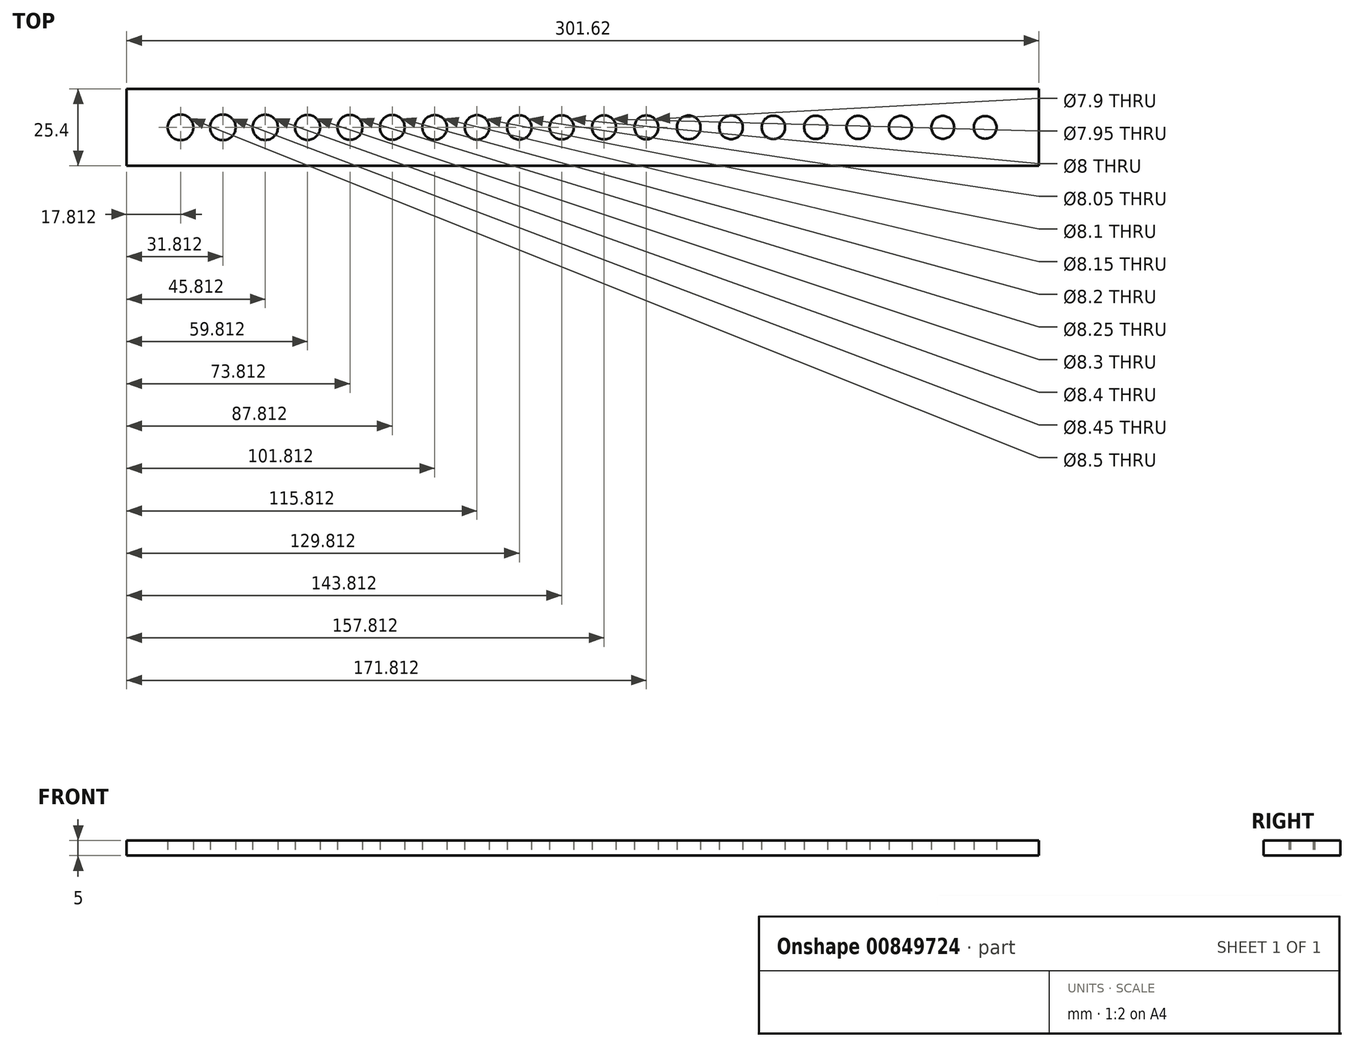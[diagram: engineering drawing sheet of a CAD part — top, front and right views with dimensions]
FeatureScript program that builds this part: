
annotation { "Feature Type Name" : "Feature", "Feature Type Description" : "" }
export const myFeature = defineFeature(function(context is Context, id is Id, definition is map)
    precondition{}
    {
        {
            var Q0;
            Q0=qCreatedBy(makeId("Top.planeOp"),FACE);
            var sketch = newSketch(context, id + "F0", { "sketchPlane" : qUnion([Q0])});
            skLineSegment(sketch, "E0.bottom", {"start": v(0, 0) * mm, "end": v(301.63, 0) * mm});
            skLineSegment(sketch, "E0.top", {"start": v(0, 25.4) * mm, "end": v(301.63, 25.4) * mm});
            skLineSegment(sketch, "E0.left", {"start": v(0, 0) * mm, "end": v(0, 25.4) * mm});
            skLineSegment(sketch, "E0.right", {"start": v(301.63, 0) * mm, "end": v(301.63, 25.4) * mm});
            skLineSegment(sketch, "E1", {"start": v(0, 12.7) * mm, "end": v(301.63, 12.7) * mm, "construction": true});
            skPoint(sketch, "E2", {"position": v(17.81, 12.7) * mm});
            skPoint(sketch, "E3.1.0.0", {"position": v(31.81, 12.7) * mm});
            skPoint(sketch, "E3.2.0.0", {"position": v(45.81, 12.7) * mm});
            skPoint(sketch, "E3.3.0.0", {"position": v(59.81, 12.7) * mm});
            skPoint(sketch, "E3.4.0.0", {"position": v(73.81, 12.7) * mm});
            skPoint(sketch, "E3.5.0.0", {"position": v(87.81, 12.7) * mm});
            skPoint(sketch, "E3.6.0.0", {"position": v(101.81, 12.7) * mm});
            skPoint(sketch, "E3.7.0.0", {"position": v(115.81, 12.7) * mm});
            skPoint(sketch, "E3.8.0.0", {"position": v(129.81, 12.7) * mm});
            skPoint(sketch, "E3.9.0.0", {"position": v(143.81, 12.7) * mm});
            skPoint(sketch, "E3.10.0.0", {"position": v(157.81, 12.7) * mm});
            skPoint(sketch, "E3.11.0.0", {"position": v(171.81, 12.7) * mm});
            skPoint(sketch, "E3.12.0.0", {"position": v(185.81, 12.7) * mm});
            skPoint(sketch, "E3.13.0.0", {"position": v(199.81, 12.7) * mm});
            skPoint(sketch, "E3.14.0.0", {"position": v(213.81, 12.7) * mm});
            skPoint(sketch, "E3.15.0.0", {"position": v(227.81, 12.7) * mm});
            skPoint(sketch, "E3.16.0.0", {"position": v(241.81, 12.7) * mm});
            skPoint(sketch, "E3.17.0.0", {"position": v(255.81, 12.7) * mm});
            skPoint(sketch, "E3.18.0.0", {"position": v(269.81, 12.7) * mm});
            skPoint(sketch, "E3.19.0.0", {"position": v(283.81, 12.7) * mm});
            skLineSegment(sketch, "E3.direction1", {"start": v(17.81, 12.7) * mm, "end": v(31.81, 12.7) * mm, "construction": true});
            skCircle(sketch, "E4", {"center": v(17.81, 12.7) * mm, "radius": 4.25 * mm});
            skCircle(sketch, "E5", {"center": v(31.81, 12.7) * mm, "radius": 4.22 * mm});
            skCircle(sketch, "E6", {"center": v(45.81, 12.7) * mm, "radius": 4.2 * mm});
            skCircle(sketch, "E7", {"center": v(59.81, 12.7) * mm, "radius": 4.15 * mm});
            skCircle(sketch, "E8", {"center": v(73.81, 12.7) * mm, "radius": 4.12 * mm});
            skCircle(sketch, "E9", {"center": v(87.81, 12.7) * mm, "radius": 4.1 * mm});
            skCircle(sketch, "E10", {"center": v(101.81, 12.7) * mm, "radius": 4.08 * mm});
            skCircle(sketch, "E11", {"center": v(115.81, 12.7) * mm, "radius": 4.05 * mm});
            skCircle(sketch, "E12", {"center": v(129.81, 12.7) * mm, "radius": 4.03 * mm});
            skCircle(sketch, "E13", {"center": v(143.81, 12.7) * mm, "radius": 4 * mm});
            skCircle(sketch, "E14", {"center": v(157.81, 12.7) * mm, "radius": 3.98 * mm});
            skCircle(sketch, "E15", {"center": v(171.81, 12.7) * mm, "radius": 3.95 * mm});
            skCircle(sketch, "E16", {"center": v(185.81, 12.7) * mm, "radius": 3.92 * mm});
            skCircle(sketch, "E17", {"center": v(199.81, 12.7) * mm, "radius": 3.9 * mm});
            skCircle(sketch, "E18", {"center": v(213.81, 12.7) * mm, "radius": 3.88 * mm});
            skCircle(sketch, "E19", {"center": v(227.81, 12.7) * mm, "radius": 3.85 * mm});
            skCircle(sketch, "E20", {"center": v(241.81, 12.7) * mm, "radius": 3.83 * mm});
            skCircle(sketch, "E21", {"center": v(255.81, 12.7) * mm, "radius": 3.8 * mm});
            skCircle(sketch, "E22", {"center": v(269.81, 12.7) * mm, "radius": 3.78 * mm});
            skCircle(sketch, "E23", {"center": v(283.81, 12.7) * mm, "radius": 3.75 * mm});
            skSolve(sketch);
        }
        {
            var Q0;
            Q0 = qSketchRegion(id + "F0", true);
            extrude(context, id + "F1", {"entities" : qUnion([Q0]), "depth" : 5 * mm, "offsetDistance" : 25 * mm});
        }
    });
